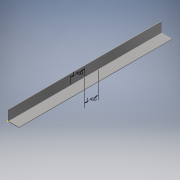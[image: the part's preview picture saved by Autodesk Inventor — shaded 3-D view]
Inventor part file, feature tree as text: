
AUTODESK INVENTOR PART (.ipt)
format: ipt  version: 2017 (Build 210142000, 142)  size: 124,928 bytes
history: native  units: in
note: dims shown in document units (in); Inventor stores cm internally (conversion verified against a paired STEP export)
features: sketch x5, extrude x3, other x3, reference x2
ambient origin geometry x8: Origin, YZ Plane, XZ Plane, XY Plane, X Axis, Y Axis, Z Axis, Center Point
bodies: Solid1 (feature_tree)
feature tree (13):
  extrude  "Extrusion1"  Depth=1.1in
  extrude  "Extrusion2"  Depth=0.06in
  sketch  "Sketch3"  dims[d5=1.1in d6=0.0in d7=1.45in]
  sketch  "Sketch4"  dims[d8=1.45in]
  extrude  "Extrusion3"  Depth=1.1in
  sketch  "Sketch1"  dims[d0=16.0in d1=1.1in]
  sketch  "Sketch2"  dims[d2=0.06in d3=0.0in d4=0.06in]
  sketch  "Sketch5"  dims[d9=0.9375in d10=0.0in]
  reference  "Reference1"
  reference  "Reference2"
  other  "Flywheel shit.iam"
  other  "Flywheel Motor Plate_MIR:1"
  other  "Flywheel Motor Plate:1"
